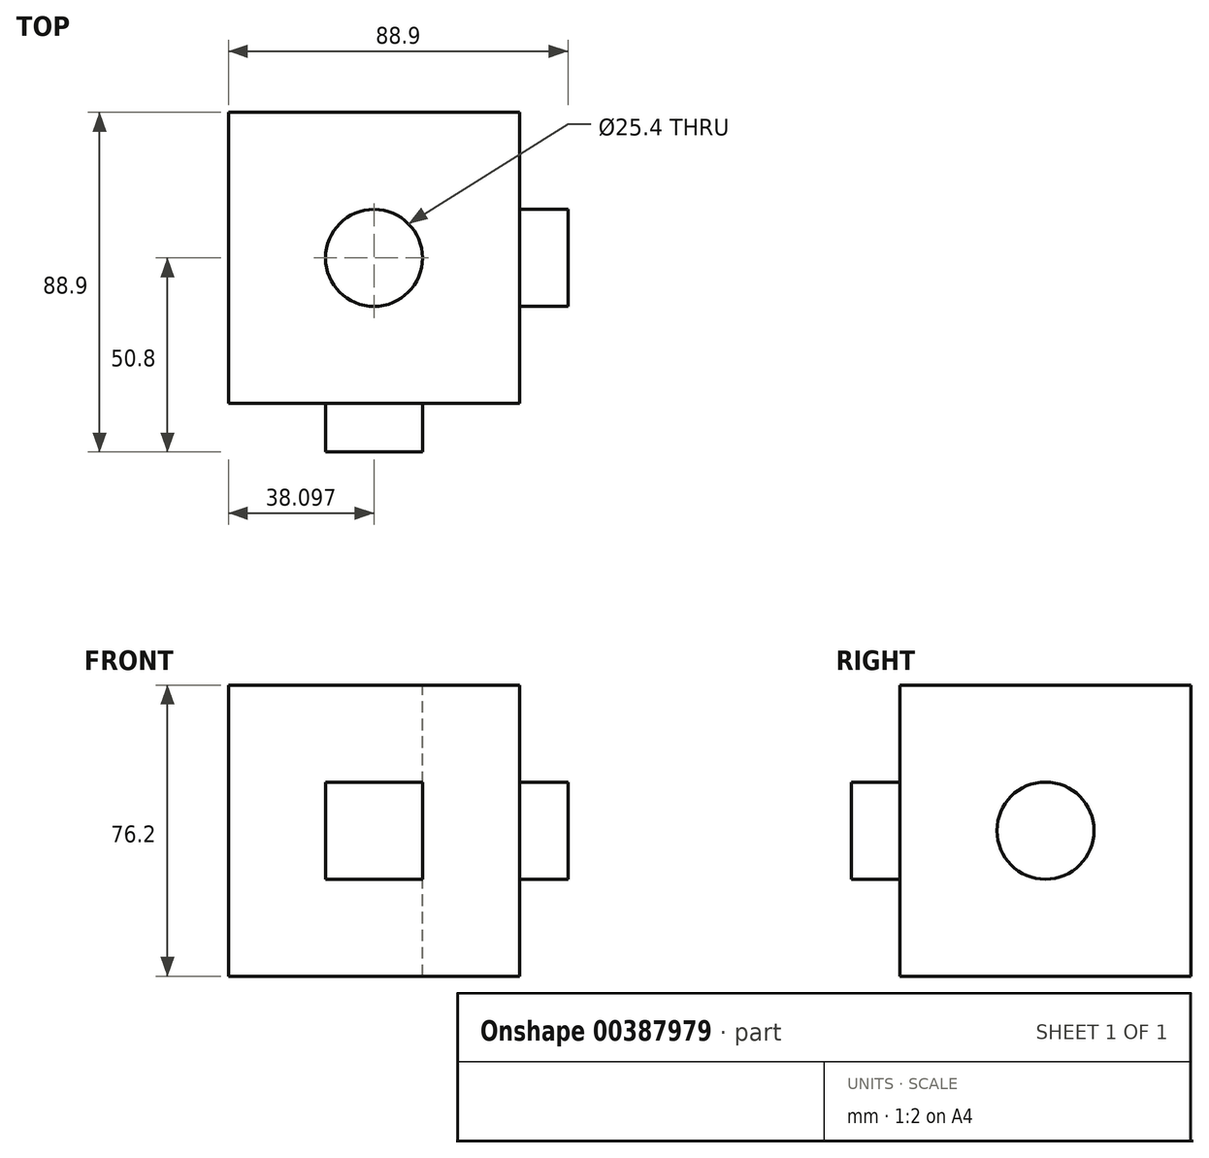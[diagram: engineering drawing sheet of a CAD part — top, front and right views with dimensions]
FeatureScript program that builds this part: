
annotation { "Feature Type Name" : "Feature", "Feature Type Description" : "" }
export const myFeature = defineFeature(function(context is Context, id is Id, definition is map)
    precondition{}
    {
        {
            var Q0;
            Q0=qCreatedBy(makeId("Front.planeOp"),FACE);
            var sketch = newSketch(context, id + "F0", { "sketchPlane" : qUnion([Q0])});
            skLineSegment(sketch, "E0.bottom", {"start": v(-130.47, -93.26) * mm, "end": v(-54.27, -93.26) * mm});
            skLineSegment(sketch, "E0.top", {"start": v(-130.47, -17.06) * mm, "end": v(-54.27, -17.06) * mm});
            skLineSegment(sketch, "E0.left", {"start": v(-130.47, -93.26) * mm, "end": v(-130.47, -17.06) * mm});
            skLineSegment(sketch, "E0.right", {"start": v(-54.27, -93.26) * mm, "end": v(-54.27, -17.06) * mm});
            skSolve(sketch);
        }
        {
            var Q0;
            Q0=makeQuery(id+"F0.imprint","IMPRINT",FACE,{"disambiguationData":[TD([[makeQuery(id+"F0.imprint","IMPRINT",EDGE,{"derivedFrom":sQuery(id+"F0.wireOp",EDGE,"E0.bottom")}),1.0]])]});
            extrude(context, id + "F1", {"entities" : qUnion([Q0]), "depth" : 76.2 * mm});
        }
        {
            var Q0;
            Q0=makeQuery(id+"F1.opExtrude","SWEPT_FACE",FACE,{"disambiguationData":[OSD([sQuery(id+"F0.wireOp",EDGE,"E0.top")])]});
            var sketch = newSketch(context, id + "F2", { "sketchPlane" : qUnion([Q0])});
            skPoint(sketch, "E1", {"position": v(-92.37, 0) * mm});
            skPoint(sketch, "E2", {"position": v(-92.37, -38.1) * mm});
            skSolve(sketch);
        }
        {
            var Q0;
            Q0=sQuery(id+"F2.wireOp",VERTEX,"E2");
            var Q1;
            Q1=makeQuery(id+"F1.opExtrude","SWEPT_BODY",BODY,{"disambiguationData":[OSD([sQuery(id+"F0.wireOp",EDGE,"E0.bottom"),sQuery(id+"F0.wireOp",EDGE,"E0.top"),sQuery(id+"F0.wireOp",EDGE,"E0.left"),sQuery(id+"F0.wireOp",EDGE,"E0.right")])]});
            hole(context, id + "F3", {"style" : HoleStyle.SIMPLE, "endStyle" : HoleEndStyle.THROUGH, "holeDiameter" : 25.4 * mm, "isTappedThrough" : true, "tappedDepth" : 12.7 * mm, "tapClearance" : 3, "locations" : qUnion([Q0]), "scope" : qUnion([Q1])});
        }
        {
            var Q0;
            Q0=makeQuery(id+"F1.opExtrude","CAP_FACE",FACE,{"disambiguationData":[OSD([sQuery(id+"F0.wireOp",EDGE,"E0.bottom"),sQuery(id+"F0.wireOp",EDGE,"E0.top"),sQuery(id+"F0.wireOp",EDGE,"E0.left"),sQuery(id+"F0.wireOp",EDGE,"E0.right")])],"isStart":false});
            var sketch = newSketch(context, id + "F4", { "sketchPlane" : qUnion([Q0])});
            skLineSegment(sketch, "E3.bottom", {"start": v(-105.07, -67.86) * mm, "end": v(-79.67, -67.86) * mm});
            skLineSegment(sketch, "E3.top", {"start": v(-105.07, -42.46) * mm, "end": v(-79.67, -42.46) * mm});
            skLineSegment(sketch, "E3.left", {"start": v(-105.07, -67.86) * mm, "end": v(-105.07, -42.46) * mm});
            skLineSegment(sketch, "E3.right", {"start": v(-79.67, -67.86) * mm, "end": v(-79.67, -42.46) * mm});
            skSolve(sketch);
        }
        {
            var Q0;
            Q0=makeQuery(id+"F4.imprint","IMPRINT",FACE,{"disambiguationData":[TD([[makeQuery(id+"F4.imprint","IMPRINT",EDGE,{"derivedFrom":sQuery(id+"F4.wireOp",EDGE,"E3.bottom")}),1.0]])]});
            extrude(context, id + "F5", {"entities" : qUnion([Q0]), "operationType" : NewBodyOperationType.ADD, "depth" : 12.7 * mm});
        }
        {
            var Q0;
            Q0=makeQuery(id+"F1.opExtrude","SWEPT_FACE",FACE,{"disambiguationData":[OSD([sQuery(id+"F0.wireOp",EDGE,"E0.right")])]});
            var sketch = newSketch(context, id + "F6", { "sketchPlane" : qUnion([Q0])});
            skCircle(sketch, "E4", {"center": v(-38.1, -55.16) * mm, "radius": 12.7 * mm});
            skSolve(sketch);
        }
        {
            var Q0;
            Q0=makeQuery(id+"F6.imprint","IMPRINT",FACE,{"disambiguationData":[TD([[makeQuery(id+"F6.imprint","IMPRINT",EDGE,{"derivedFrom":sQuery(id+"F6.wireOp",EDGE,"E4")}),1.0]])]});
            extrude(context, id + "F7", {"entities" : qUnion([Q0]), "operationType" : NewBodyOperationType.ADD, "depth" : 12.7 * mm});
        }
    });
